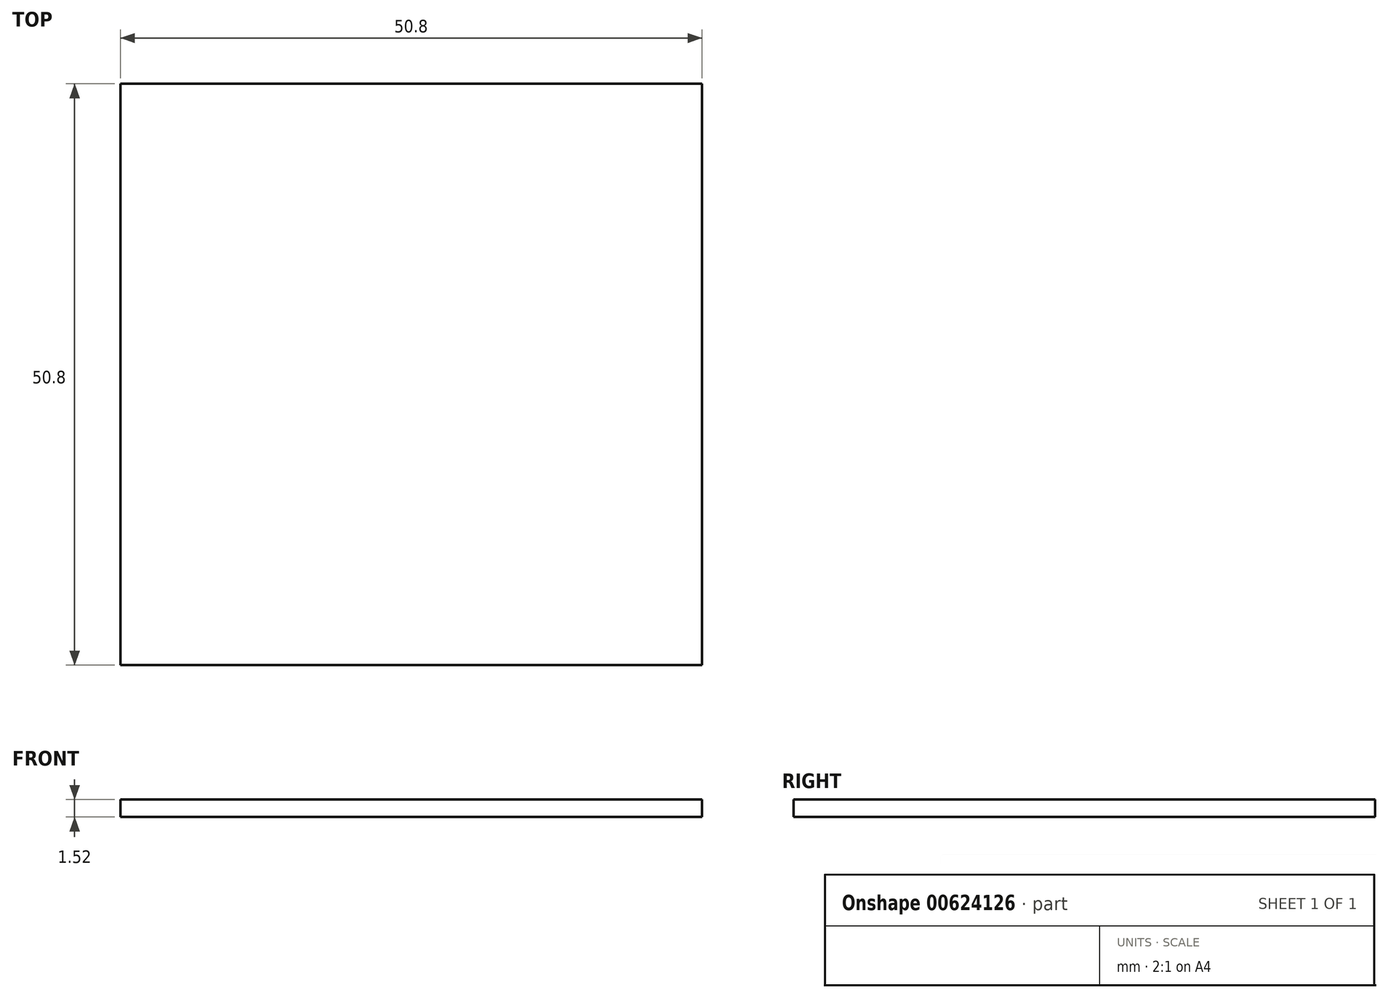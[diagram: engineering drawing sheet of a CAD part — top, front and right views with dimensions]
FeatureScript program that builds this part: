
annotation { "Feature Type Name" : "Feature", "Feature Type Description" : "" }
export const myFeature = defineFeature(function(context is Context, id is Id, definition is map)
    precondition{}
    {
        {
            var Q0;
            Q0=qCreatedBy(makeId("Top.planeOp"),FACE);
            var sketch = newSketch(context, id + "F0", { "sketchPlane" : qUnion([Q0])});
            skLineSegment(sketch, "E0.bottom", {"start": v(25.4, 25.4) * mm, "end": v(-25.4, 25.4) * mm});
            skLineSegment(sketch, "E0.top", {"start": v(25.4, -25.4) * mm, "end": v(-25.4, -25.4) * mm});
            skLineSegment(sketch, "E0.left", {"start": v(25.4, 25.4) * mm, "end": v(25.4, -25.4) * mm});
            skLineSegment(sketch, "E0.right", {"start": v(-25.4, 25.4) * mm, "end": v(-25.4, -25.4) * mm});
            skPoint(sketch, "E0.middle", {"position": v(0, 0) * mm});
            skSolve(sketch);
        }
        {
            var Q0;
            Q0 = qSketchRegion(id + "F0", true);
            extrude(context, id + "F1", {"entities" : qUnion([Q0]), "endBound" : BoundingType.SYMMETRIC, "depth" : 1.52 * mm, "offsetDistance" : 25.4 * mm});
        }
    });
